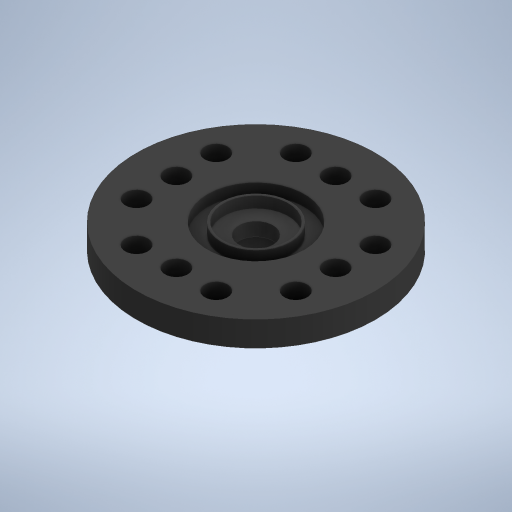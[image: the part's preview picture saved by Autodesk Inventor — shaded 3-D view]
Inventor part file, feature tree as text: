
AUTODESK INVENTOR PART (.ipt)
format: ipt  version: 2023.1 (Build 271208000, 208)  size: 305,152 bytes
history: native  units: mm
features: extrude x4, sketch x4, other x1, pattern_circular x1
ambient origin geometry x8: Origin, YZ Plane, XZ Plane, XY Plane, X Axis, Y Axis, Z Axis, Center Point
bodies: Body1 (feature_tree)
feature tree (10):
  other  "솔리드1"
  extrude  "돌출1"  Depth=8.7mm
  extrude  "돌출2"  Depth=5.5mm
  extrude  "돌출3"  Depth=3.0mm TaperAngle=0.0deg
  extrude  "돌출4"  Depth=21.0mm
  pattern_circular  "원형 패턴1"  [2 undecoded]
  sketch  "스케치1"
  sketch  "스케치3"
  sketch  "스케치4"
  sketch  "스케치5"
note: 2 required parameter values undecoded (feature->parameter linkage not recoverable at this tier; creation-order binding heuristic only, values carry confidence <= 0.55)
